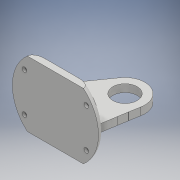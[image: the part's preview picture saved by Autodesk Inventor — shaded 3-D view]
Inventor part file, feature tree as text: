
AUTODESK INVENTOR PART (.ipt)
format: ipt  version: 2017 (Build 210142000, 142)  size: 480,768 bytes
history: native  units: mm
features: reference x4, sketch x3, extrude x2, fillet x2, hole x1
ambient origin geometry x8: Origin, YZ Plane, XZ Plane, XY Plane, X Axis, Y Axis, Z Axis, Center Point
bodies: Solid1 (feature_tree)
feature tree (12):
  extrude  "Extrusion1"  Depth=6.0mm TaperAngle=0.0deg
  extrude  "Extrusion2"  Depth=4.0mm
  fillet  "Fillet1"  Radius=4.3mm
  fillet  "Fillet3"  Radius=4.3mm
  hole  "Hole1"  [1 undecoded]
  sketch  "Sketch1"  dims[d1=0.0mm d2=6.0mm d3=0.0mm]
  reference  "Reference6"
  reference  "Reference7"
  sketch  "Sketch2"  dims[d4=6.0mm d6=4.0mm d7=4.3mm d8=4.3mm]
  reference  "Reference8"
  reference  "Reference9"
  sketch  "Sketch3"  dims[d9=4.3mm d10=6.0mm d11=8.0mm d12=3.5mm d13=90.0deg d14=8.0mm d15=20.594885mm d16=4.3mm d17=4.3mm d21=22.3mm]
note: 1 required parameter value undecoded (feature->parameter linkage not recoverable at this tier; creation-order binding heuristic only, values carry confidence <= 0.55)
